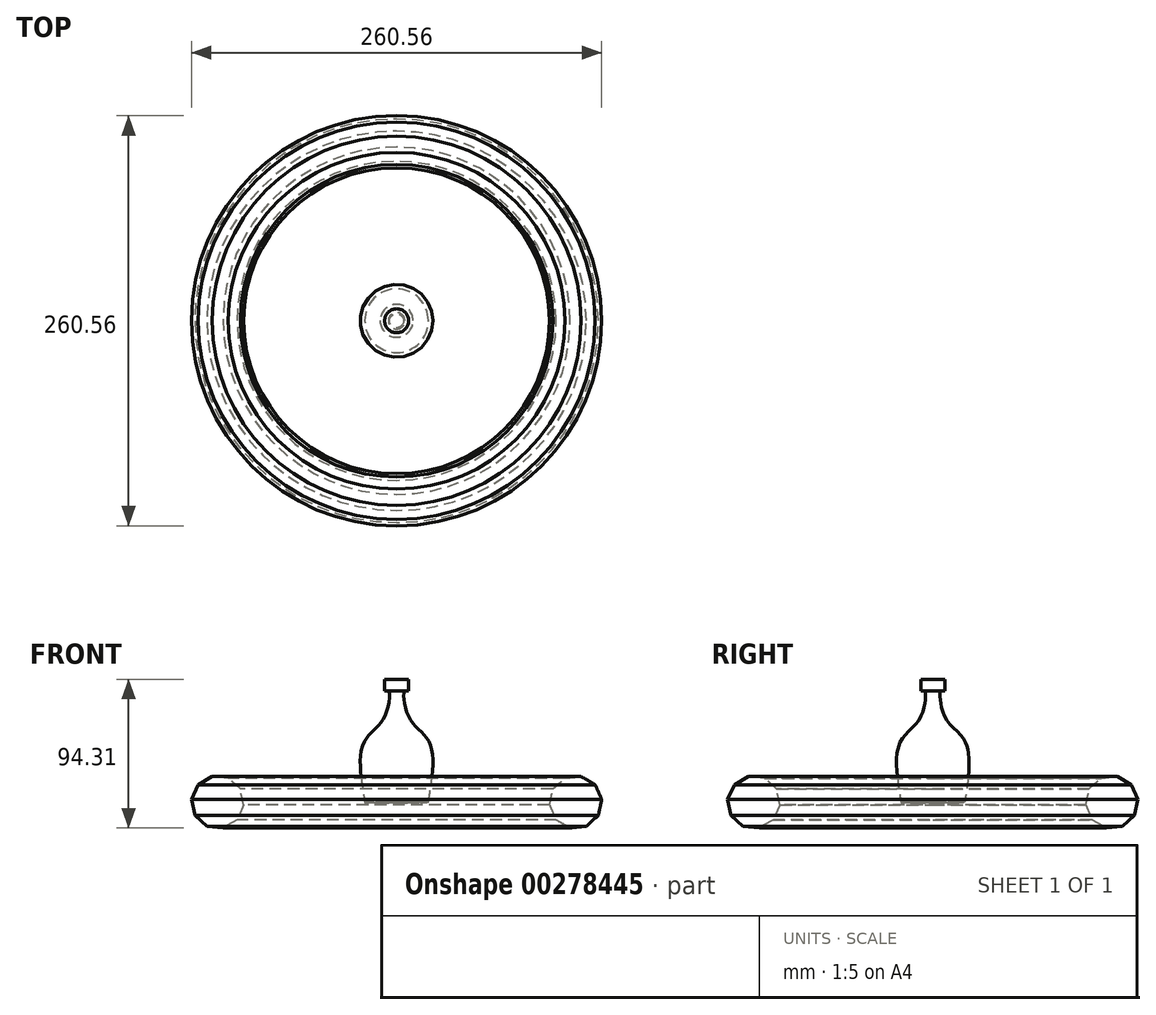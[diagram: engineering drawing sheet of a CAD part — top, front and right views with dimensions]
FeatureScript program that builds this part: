
annotation { "Feature Type Name" : "Feature", "Feature Type Description" : "" }
export const myFeature = defineFeature(function(context is Context, id is Id, definition is map)
    precondition{}
    {
        {
            var Q0;
            Q0=qCreatedBy(makeId("Front.planeOp"),FACE);
            var sketch = newSketch(context, id + "F0", { "sketchPlane" : qUnion([Q0])});
            skLineSegment(sketch, "E0", {"start": v(0, 76.29) * mm, "end": v(0, -77.25) * mm, "construction": true});
            skCircle(sketch, "E1.cCircle", {"center": v(-113.7, 0) * mm, "radius": 15.85 * mm, "construction": true});
            skLineSegment(sketch, "E1.0", {"start": v(-101.3, -11.14) * mm, "end": v(-110.21, -16.3) * mm});
            skLineSegment(sketch, "E1.1", {"start": v(-110.21, -16.3) * mm, "end": v(-120.46, -15.24) * mm});
            skLineSegment(sketch, "E1.2", {"start": v(-120.46, -15.24) * mm, "end": v(-128.12, -8.35) * mm});
            skLineSegment(sketch, "E1.3", {"start": v(-128.12, -8.35) * mm, "end": v(-130.28, 1.72) * mm});
            skLineSegment(sketch, "E1.4", {"start": v(-130.28, 1.72) * mm, "end": v(-126.1, 11.14) * mm});
            skLineSegment(sketch, "E1.5", {"start": v(-126.1, 11.14) * mm, "end": v(-117.18, 16.3) * mm});
            skLineSegment(sketch, "E1.6", {"start": v(-117.18, 16.3) * mm, "end": v(-106.93, 15.24) * mm});
            skLineSegment(sketch, "E1.7", {"start": v(-106.93, 15.24) * mm, "end": v(-99.27, 8.35) * mm});
            skLineSegment(sketch, "E1.8", {"start": v(-99.27, 8.35) * mm, "end": v(-97.12, -1.72) * mm});
            skLineSegment(sketch, "E1.9", {"start": v(-97.12, -1.72) * mm, "end": v(-101.3, -11.14) * mm});
            skPoint(sketch, "E1.0.midPoint", {"position": v(-105.76, -13.72) * mm});
            skSolve(sketch);
        }
        {
            var Q0;
            Q0=qCreatedBy(makeId("Front.planeOp"),FACE);
            var sketch = newSketch(context, id + "F1", { "sketchPlane" : qUnion([Q0])});
            skFitSpline(sketch, "E2", {"points": [v(-20.2, 0) * mm, v(-20.88, 37.82) * mm, v(-7.93, 53.67) * mm, v(-4.8, 70.19) * mm, v(-5.53, 70.9) * mm], "startDerivative": vector(-18.22, 112.48) * mm, "endDerivative": vector(-12.72, 4.94) * mm});
            skLineSegment(sketch, "E3", {"start": v(-5.29, 70.8) * mm, "end": v(-7.62, 70.8) * mm});
            skLineSegment(sketch, "E4", {"start": v(-7.62, 70.8) * mm, "end": v(-7.62, 78) * mm});
            skLineSegment(sketch, "E5", {"start": v(-7.62, 78) * mm, "end": v(0, 78) * mm});
            skLineSegment(sketch, "E6", {"start": v(0, 78) * mm, "end": v(0, 1.8) * mm});
            skLineSegment(sketch, "E7", {"start": v(0, 1.8) * mm, "end": v(-10.46, -0.2) * mm});
            skFitSpline(sketch, "E8", {"points": [v(-20.2, 0) * mm, v(-15.9, 0) * mm, v(-10.46, -0.2) * mm], "startDerivative": vector(9.05, -0.73) * mm, "endDerivative": vector(10.4, 3.96) * mm});
            skLineSegment(sketch, "E9", {"start": v(0, 81.8) * mm, "end": v(0, -6.28) * mm, "construction": true});
            skSolve(sketch);
        }
        {
            var Q0;
            Q0 = qSketchRegion(id + "F1", true);
            var Q1;
            Q1=sQuery(id+"F1.wireOp",EDGE,"E6");
            revolve(context, id + "F2", {"entities" : qUnion([Q0]), "axis" : qUnion([Q1]), "revolveType" : RevolveType.FULL});
        }
        {
            var Q0;
            Q0=makeQuery(id+"F0.imprint","IMPRINT",FACE,{"disambiguationData":[TD([[makeQuery(id+"F0.imprint","IMPRINT",EDGE,{"derivedFrom":sQuery(id+"F0.wireOp",EDGE,"E1.0")}),-1.0]])]});
            var Q1;
            Q1=sQuery(id+"F0.wireOp",EDGE,"E0");
            revolve(context, id + "F3", {"entities" : qUnion([Q0]), "axis" : qUnion([Q1]), "revolveType" : RevolveType.FULL});
        }
    });
